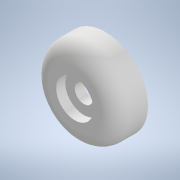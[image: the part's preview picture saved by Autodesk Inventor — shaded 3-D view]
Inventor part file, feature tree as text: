
AUTODESK INVENTOR PART (.ipt)
format: ipt  version: 2022 (Build 260153070, 153G)  size: 163,840 bytes
history: native  units: mm
features: other x4, sketch x3, extrude x3, reference x3, plane x1, fillet x1
ambient origin geometry x8: Origin, YZ Plane, XZ Plane, XY Plane, X Axis, Y Axis, Z Axis, Center Point
bodies: Solid1 (feature_tree)
feature tree (15):
  sketch  "Sketch1"  dims[d0=0.2mm d1=0.0mm d2=1.15mm d3=0.0mm]
  plane  "Work Plane1"
  extrude  "Extrusion1"  Depth=1.15mm TaperAngle=0.0deg
  extrude  "Extrusion2"  Depth=1.75mm
  fillet  "Fillet1"  Radius=4.1mm
  extrude  "Extrusion3"  [1 undecoded]
  reference  "Reference1"
  reference  "Reference2"
  sketch  "Sketch2"  dims[d4=2.0mm d5=0.0mm d6=1.75mm d7=4.1mm]
  reference  "Reference7"
  sketch  "Sketch3"  dims[d8=1.0mm d9=0.0mm]
  other  "<userpath> laptop\Desktop\SumoBot\sumobotENCODER\MotorEncoderAssembly.iam"
  other  "MotorEncoderAssembly.iam"
  other  "TTencoderspacer:1"
  other  "TT motor output:1"
note: 1 required parameter value undecoded (feature->parameter linkage not recoverable at this tier; creation-order binding heuristic only, values carry confidence <= 0.55)
